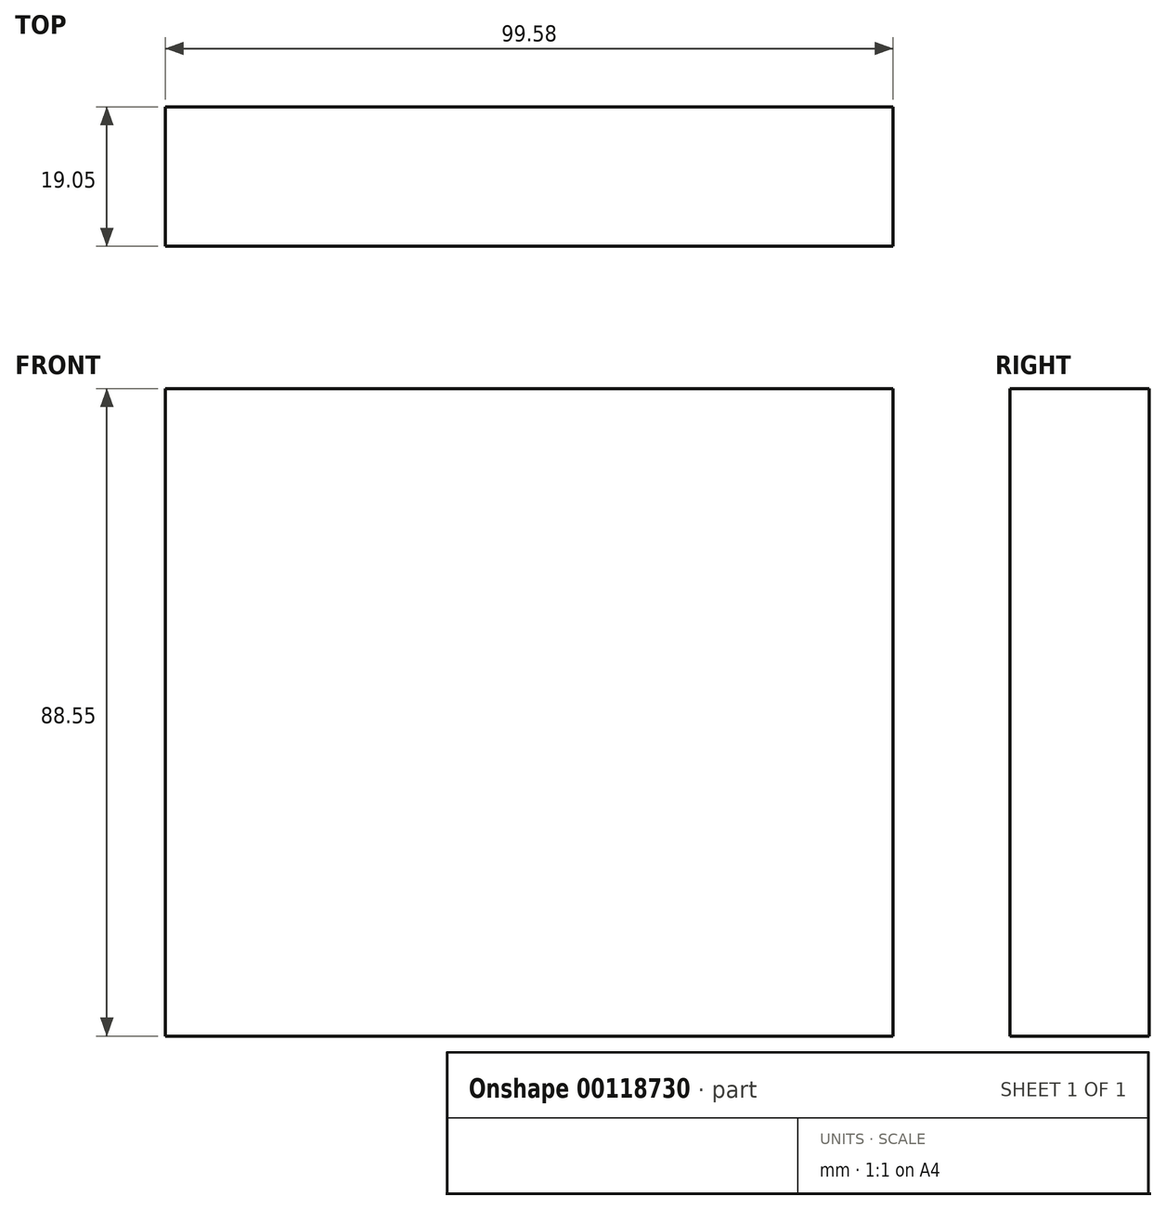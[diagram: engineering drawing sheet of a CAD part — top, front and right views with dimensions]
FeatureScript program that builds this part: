
annotation { "Feature Type Name" : "Feature", "Feature Type Description" : "" }
export const myFeature = defineFeature(function(context is Context, id is Id, definition is map)
    precondition{}
    {
        {
            var Q0;
            Q0=qCreatedBy(makeId("Front.planeOp"),FACE);
            var sketch = newSketch(context, id + "F0", { "sketchPlane" : qUnion([Q0])});
            skLineSegment(sketch, "E0.bottom", {"start": v(0, 0) * mm, "end": v(99.58, 0) * mm});
            skLineSegment(sketch, "E0.top", {"start": v(0, 88.55) * mm, "end": v(99.58, 88.55) * mm});
            skLineSegment(sketch, "E0.left", {"start": v(0, 0) * mm, "end": v(0, 88.55) * mm});
            skLineSegment(sketch, "E0.right", {"start": v(99.58, 0) * mm, "end": v(99.58, 88.55) * mm});
            skSolve(sketch);
        }
        {
            var Q0;
            Q0 = qSketchRegion(id + "F0", true);
            extrude(context, id + "F1", {"entities" : qUnion([Q0]), "depth" : 19.05 * mm});
        }
    });
